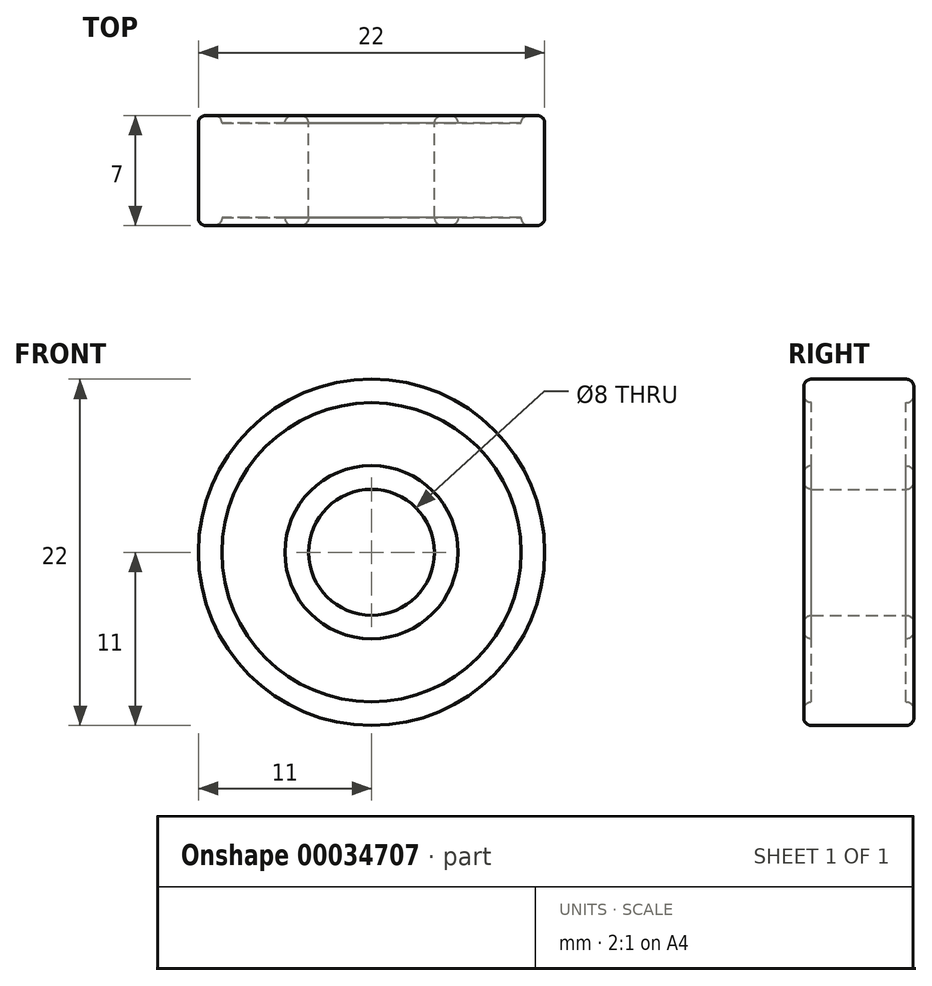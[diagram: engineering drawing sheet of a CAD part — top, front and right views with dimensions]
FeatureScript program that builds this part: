
annotation { "Feature Type Name" : "Feature", "Feature Type Description" : "" }
export const myFeature = defineFeature(function(context is Context, id is Id, definition is map)
    precondition{}
    {
        {
            var Q0;
            Q0=qCreatedBy(makeId("Front.planeOp"),FACE);
            var sketch = newSketch(context, id + "F0", { "sketchPlane" : qUnion([Q0])});
            skCircle(sketch, "E0", {"center": v(0, 0) * mm, "radius": 4 * mm});
            skCircle(sketch, "E1", {"center": v(0, 0) * mm, "radius": 11 * mm});
            skCircle(sketch, "E2", {"center": v(0, 0) * mm, "radius": 5.5 * mm});
            skCircle(sketch, "E3", {"center": v(0, 0) * mm, "radius": 9.5 * mm});
            skSolve(sketch);
        }
        {
            var Q0;
            Q0=makeQuery(id+"F0.imprint","IMPRINT",FACE,{"disambiguationData":[TD([[makeQuery(id+"F0.imprint","IMPRINT",EDGE,{"derivedFrom":sQuery(id+"F0.wireOp",EDGE,"E1")}),1.0]])]});
            var Q1;
            Q1=makeQuery(id+"F0.imprint","IMPRINT",FACE,{"disambiguationData":[TD([[makeQuery(id+"F0.imprint","IMPRINT",EDGE,{"derivedFrom":sQuery(id+"F0.wireOp",EDGE,"E0")}),-1.0]])]});
            extrude(context, id + "F1", {"entities" : qUnion([Q0, Q1]), "endBound" : BoundingType.SYMMETRIC, "depth" : 7 * mm});
        }
        {
            var Q0;
            Q0=makeQuery(id+"F0.imprint","IMPRINT",FACE,{"disambiguationData":[TD([[makeQuery(id+"F0.imprint","IMPRINT",EDGE,{"derivedFrom":sQuery(id+"F0.wireOp",EDGE,"E2")}),-1.0]])]});
            extrude(context, id + "F2", {"entities" : qUnion([Q0]), "operationType" : NewBodyOperationType.ADD, "endBound" : BoundingType.SYMMETRIC, "depth" : 6 * mm});
        }
        {
            var Q0;
            Q0=makeQuery(id+"F1.opExtrude","CAP_FACE",FACE,{"disambiguationData":[OSD([sQuery(id+"F0.wireOp",EDGE,"E1"),sQuery(id+"F0.wireOp",EDGE,"E3")])],"isStart":false});
            var Q1;
            Q1=makeQuery(id+"F1.opExtrude","CAP_FACE",FACE,{"disambiguationData":[OSD([sQuery(id+"F0.wireOp",EDGE,"E0"),sQuery(id+"F0.wireOp",EDGE,"E2")])],"isStart":false});
            var Q2;
            Q2=makeQuery(id+"F1.opExtrude","CAP_FACE",FACE,{"disambiguationData":[OSD([sQuery(id+"F0.wireOp",EDGE,"E1"),sQuery(id+"F0.wireOp",EDGE,"E3")])],"isStart":true});
            var Q3;
            Q3=makeQuery(id+"F1.opExtrude","CAP_FACE",FACE,{"disambiguationData":[OSD([sQuery(id+"F0.wireOp",EDGE,"E0"),sQuery(id+"F0.wireOp",EDGE,"E2")])],"isStart":true});
            fillet(context, id + "F3", {"entities" : qUnion([Q0, Q1, Q2, Q3]), "radius" : .5 * mm, "tangentPropagation" : true, "allowEdgeOverflow" : false});
        }
    });
